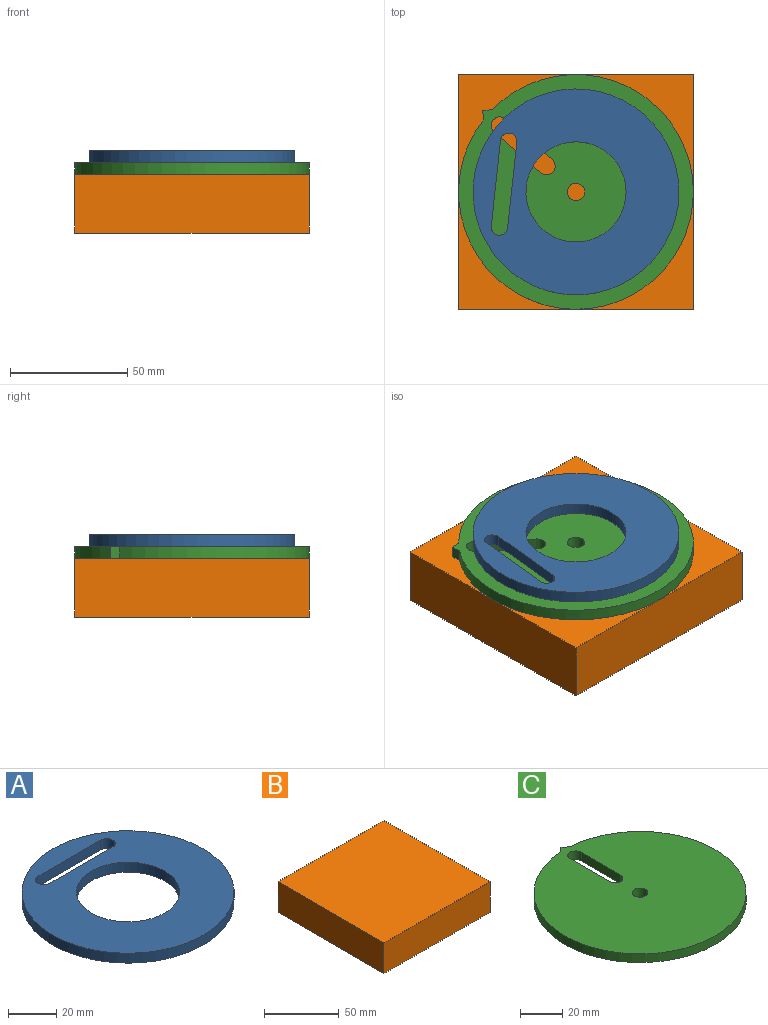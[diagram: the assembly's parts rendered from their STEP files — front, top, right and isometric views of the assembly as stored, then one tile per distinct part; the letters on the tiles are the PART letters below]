
ASSEMBLY  parts=3 mates=2
PART A: 8 faces, bbox 87.7x87.7x5 mm
  f0: cylinder r=3.5mm len=7mm, axis (0,0,-1), area 55mm2, adj f1,f4,f6,f7
  f1: plane 36.75x5mm, normal (0,-1,0), area 183.7mm2, adj f0,f2,f6,f7
  f2: cylinder r=3.5mm len=7mm, axis (0,0,-1), area 55mm2, adj f1,f4,f6,f7
  f3: cylinder r=43.87mm len=87.75mm, axis (0,0,-1), area 1378.3mm2, adj f6,f7
  f4: plane 36.75x5mm, normal (0,1,0), area 183.7mm2, adj f0,f2,f6,f7
  f5: cylinder r=21.33mm len=42.67mm, axis (0,0,-1), area 670.2mm2, adj f6,f7
  f6: plane 87.75x87.75mm, normal (0,0,1), area 4321.8mm2, adj f0,f1,f2,f3,f4,f5
  f7: plane 87.75x87.75mm, normal (0,0,-1), area 4321.8mm2, adj f0,f1,f2,f3,f4,f5
PART B: 6 faces, bbox 100x100x25 mm
  f0: plane 100x25mm, normal (-1,0,0), area 2500mm2, adj f1,f3,f4,f5
  f1: plane 100x25mm, normal (0,1,0), area 2500mm2, adj f0,f2,f4,f5
  f2: plane 100x25mm, normal (1,0,0), area 2500mm2, adj f1,f3,f4,f5
  f3: plane 100x25mm, normal (0,-1,0), area 2500mm2, adj f0,f2,f4,f5
  f4: plane 100x100mm, normal (0,0,-1), area 10000mm2, adj f0,f1,f2,f3
  f5: plane 100x100mm, normal (0,0,1), area 10000mm2, adj f0,f1,f2,f3
PART C: 10 faces, bbox 100x102.7x5 mm
  f0: cylinder r=50mm len=100mm, axis (0,0,-1), area 1541.8mm2, adj f1,f7,f8,f9
  f1: plane 5x2.89mm, normal (0.69,0.72,0), area 20.1mm2, adj f0,f7,f8,f9
  f2: plane 26.36x5mm, normal (1,0,0), area 131.8mm2, adj f3,f6,f8,f9
  f3: cylinder r=3.69mm len=7.37mm, axis (0,0,-1), area 57.9mm2, adj f2,f4,f8,f9
  f4: plane 26.36x5mm, normal (-1,0,0), area 131.8mm2, adj f3,f6,f8,f9
  f5: cylinder r=3.69mm len=7.37mm, axis (0,0,-1), area 115.8mm2, adj f8,f9
  f6: cylinder r=3.69mm len=7.37mm, axis (0,0,-1), area 57.9mm2, adj f2,f4,f8,f9
  f7: plane 5x2.89mm, normal (-0.69,0.72,0), area 20.1mm2, adj f0,f1,f8,f9
  f8: plane 102.71x100mm, normal (0,0,1), area 7581.9mm2, adj f0,f1,f2,f3,f4,f5,f6,f7
  f9: plane 102.71x100mm, normal (0,0,-1), area 7581.9mm2, adj f0,f1,f2,f3,f4,f5,f6,f7
PLACE A rot(axis=(0,0,1),83.8deg) t=(-13.12,-22.75,-4.91)mm
PLACE B t=(-13.12,-22.75,-4.91)mm fixed
PLACE C rot(axis=(0,0,1),48.8deg) t=(-13.12,-22.75,-4.91)mm
MATE revolute C.f5 <-> B.f5  axis (0,0,-1) through (-13.12,-22.75,-4.91)mm
MATE planar C.f5 <-> A.f5  axis (0,0,1) through (-13.12,-22.75,0.09)mm
